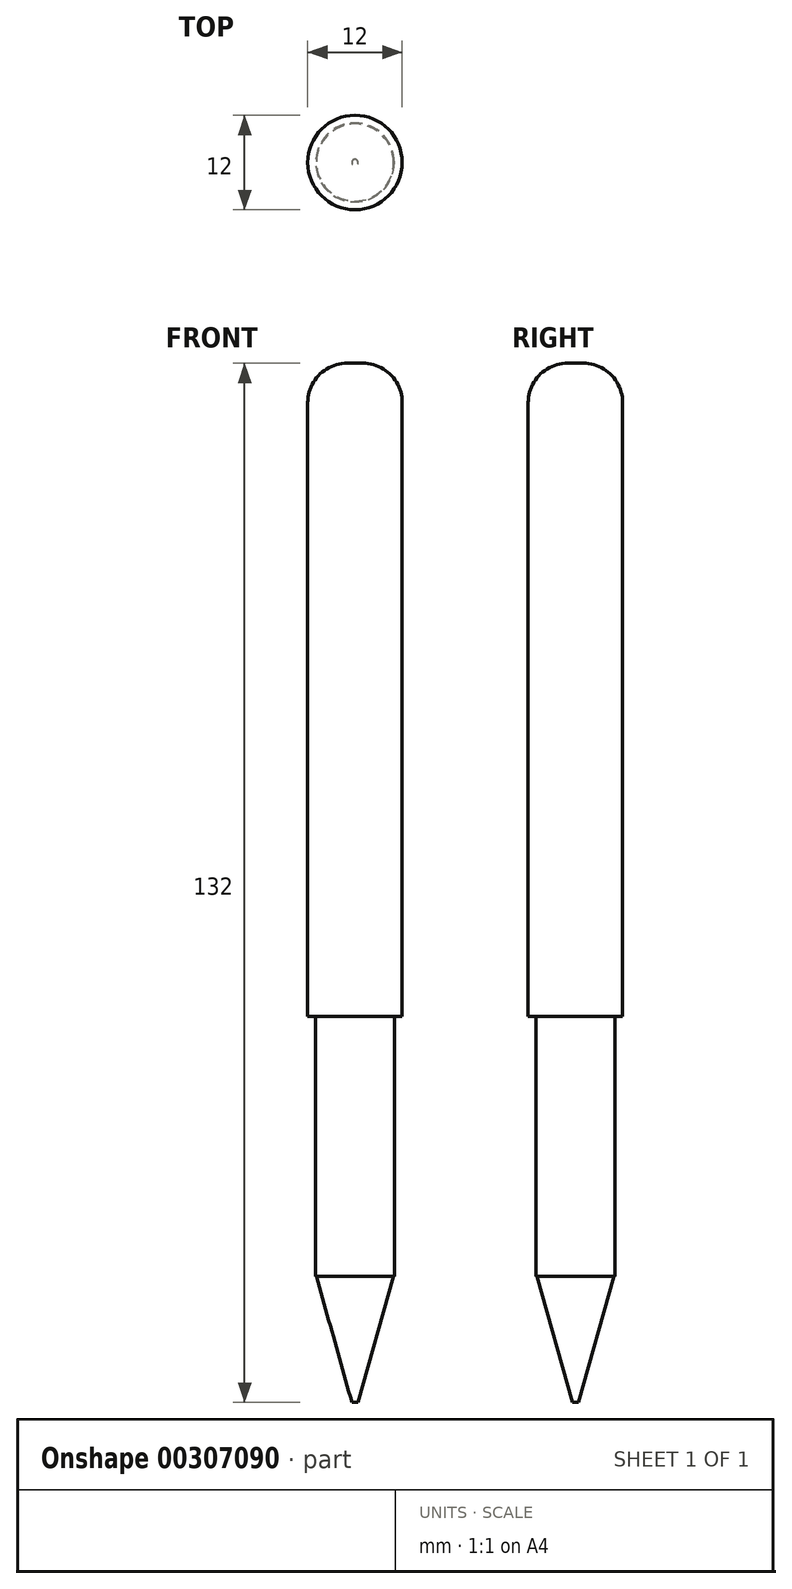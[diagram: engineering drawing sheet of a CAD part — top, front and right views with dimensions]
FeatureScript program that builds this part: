
annotation { "Feature Type Name" : "Feature", "Feature Type Description" : "" }
export const myFeature = defineFeature(function(context is Context, id is Id, definition is map)
    precondition{}
    {
        {
            var Q0;
            Q0=qCreatedBy(makeId("Top.planeOp"),FACE);
            var sketch = newSketch(context, id + "F0", { "sketchPlane" : qUnion([Q0])});
            skCircle(sketch, "E0", {"center": v(0, 0) * mm, "radius": 5 * mm});
            skSolve(sketch);
        }
        {
            var Q0;
            Q0=makeQuery(id+"F0.imprint","IMPRINT",FACE,{"disambiguationData":[TD([[makeQuery(id+"F0.imprint","IMPRINT",EDGE,{"derivedFrom":sQuery(id+"F0.wireOp",EDGE,"E0")}),1.0]])]});
            extrude(context, id + "F1", {"entities" : qUnion([Q0]), "depth" : 33 * mm});
        }
        {
            var Q0;
            Q0=makeQuery(id+"F1.opExtrude","CAP_FACE",FACE,{"disambiguationData":[OSD([sQuery(id+"F0.wireOp",EDGE,"E0")])],"isStart":true});
            var sketch = newSketch(context, id + "F2", { "sketchPlane" : qUnion([Q0])});
            skCircle(sketch, "E1.0", {"center": v(0, 0) * mm, "radius": 5 * mm});
            skCircle(sketch, "E2", {"center": v(0, 0) * mm, "radius": 4.9 * mm});
            skSolve(sketch);
        }
        {
            var Q0;
            Q0=makeQuery(id+"F2.imprint","IMPRINT",FACE,{"disambiguationData":[TD([[makeQuery(id+"F2.imprint","IMPRINT",EDGE,{"derivedFrom":sQuery(id+"F2.wireOp",EDGE,"E2")}),1.0]])]});
            extrude(context, id + "F3", {"entities" : qUnion([Q0]), "operationType" : NewBodyOperationType.ADD, "depth" : (49 - 33) * mm});
        }
        {
            var Q0;
            Q0=makeQuery(id+"F3.opExtrude","CAP_EDGE",EDGE,{"disambiguationData":[OSD([sQuery(id+"F2.wireOp",EDGE,"E2")])],"isStart":false});
            chamfer(context, id + "F4", {"entities" : qUnion([Q0]), "chamferType" : ChamferType.TWO_OFFSETS, "width1" : 4.5 * mm, "oppositeDirection" : false, "width2" : (49 - 33) * mm, "tangentPropagation" : true});
        }
        {
            var Q0;
            Q0=makeQuery(id+"F1.opExtrude","CAP_FACE",FACE,{"disambiguationData":[OSD([sQuery(id+"F0.wireOp",EDGE,"E0")])],"isStart":false});
            var sketch = newSketch(context, id + "F5", { "sketchPlane" : qUnion([Q0])});
            skCircle(sketch, "E3", {"center": v(0, 0) * mm, "radius": 6 * mm});
            skSolve(sketch);
        }
        {
            var Q0;
            Q0=makeQuery(id+"F5.imprint","IMPRINT",FACE,{"disambiguationData":[TD([[makeQuery(id+"F5.imprint","IMPRINT",EDGE,{"derivedFrom":makeQuery(id+"F1.opExtrude","CAP_EDGE",EDGE,{"disambiguationData":[OSD([sQuery(id+"F0.wireOp",EDGE,"E0")])],"isStart":false})}),1.0]])]});
            var Q1;
            Q1=makeQuery(id+"F5.imprint","IMPRINT",FACE,{"disambiguationData":[TD([[makeQuery(id+"F5.imprint","IMPRINT",EDGE,{"derivedFrom":sQuery(id+"F5.wireOp",EDGE,"E3")}),1.0]])]});
            var Q2;
            Q2=sQuery(id+"F5.wireOp",EDGE,"E3");
            extrude(context, id + "F6", {"entities" : qUnion([Q0, Q1]), "operationType" : NewBodyOperationType.ADD, "surfaceEntities" : qUnion([Q2]), "depth" : 83 * mm});
        }
        {
            var Q0;
            Q0=makeQuery(id+"F6.opExtrude","CAP_EDGE",EDGE,{"disambiguationData":[OSD([sQuery(id+"F5.wireOp",EDGE,"E3")])],"isStart":false});
            fillet(context, id + "F7", {"entities" : qUnion([Q0]), "radius" : 5 * mm, "tangentPropagation" : true, "allowEdgeOverflow" : false});
        }
    });
